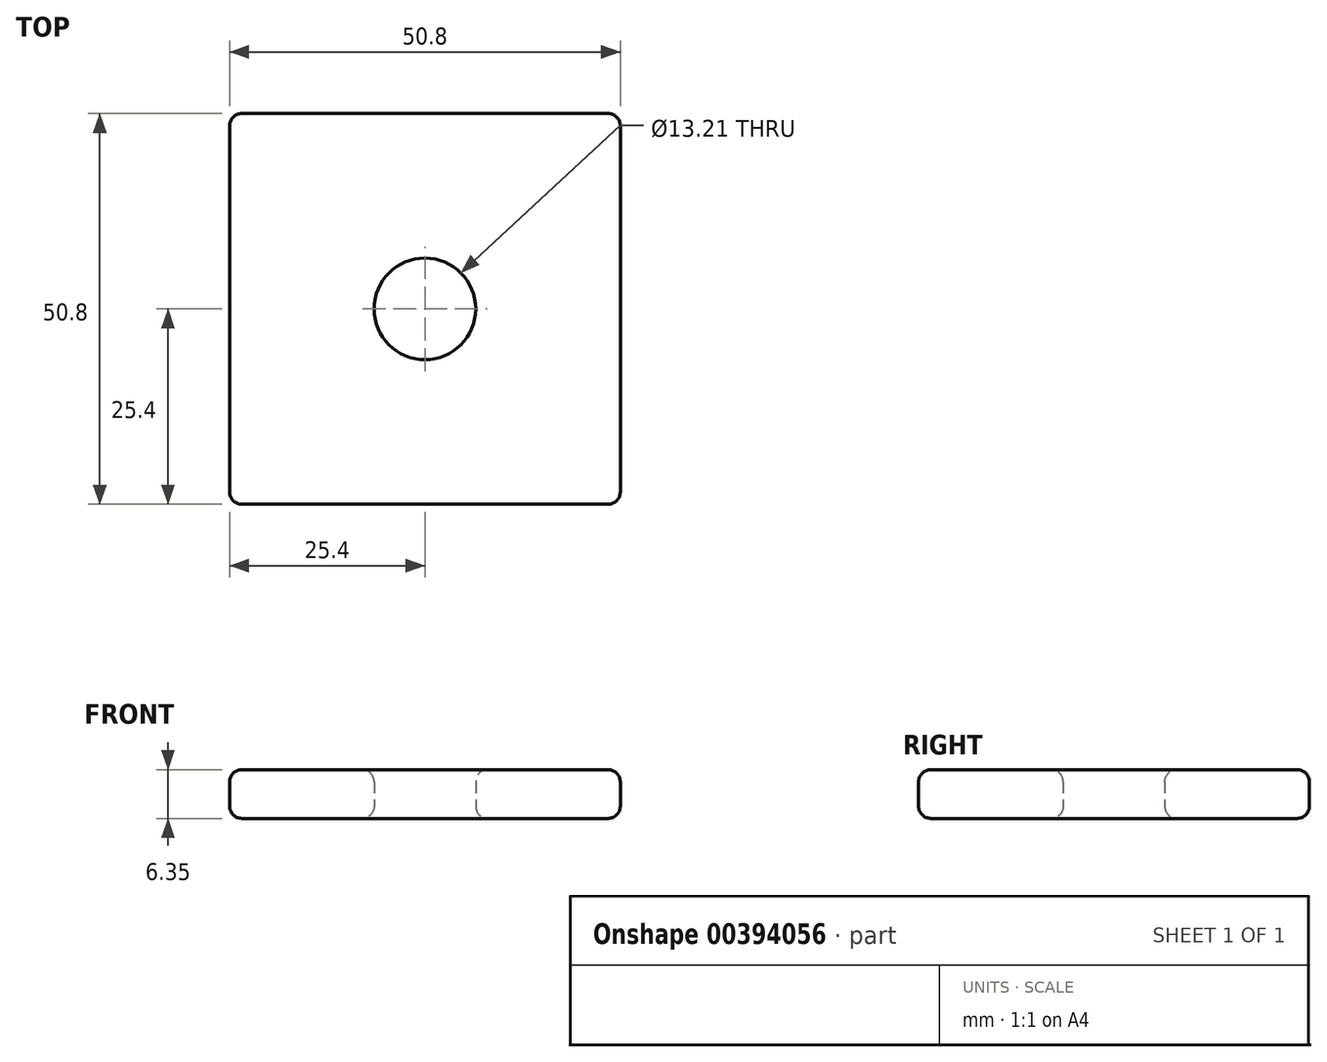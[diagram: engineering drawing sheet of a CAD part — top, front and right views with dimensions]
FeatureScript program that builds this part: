
annotation { "Feature Type Name" : "Feature", "Feature Type Description" : "" }
export const myFeature = defineFeature(function(context is Context, id is Id, definition is map)
    precondition{}
    {
        {
            var Q0;
            Q0=qCreatedBy(makeId("Top.planeOp"),FACE);
            var sketch = newSketch(context, id + "F0", { "sketchPlane" : qUnion([Q0])});
            skLineSegment(sketch, "E0.bottom", {"start": v(-25.4, 25.4) * mm, "end": v(25.4, 25.4) * mm});
            skLineSegment(sketch, "E0.top", {"start": v(-25.4, -25.4) * mm, "end": v(25.4, -25.4) * mm});
            skLineSegment(sketch, "E0.left", {"start": v(-25.4, 25.4) * mm, "end": v(-25.4, -25.4) * mm});
            skLineSegment(sketch, "E0.right", {"start": v(25.4, 25.4) * mm, "end": v(25.4, -25.4) * mm});
            skPoint(sketch, "E0.middle", {"position": v(0, 0) * mm});
            skCircle(sketch, "E1", {"center": v(0, 0) * mm, "radius": 6.6 * mm});
            skSolve(sketch);
        }
        {
            var Q0;
            Q0=makeQuery(id+"F0.imprint","IMPRINT",FACE,{"disambiguationData":[TD([[makeQuery(id+"F0.imprint","IMPRINT",EDGE,{"derivedFrom":sQuery(id+"F0.wireOp",EDGE,"E0.bottom")}),-1.0]])]});
            extrude(context, id + "F1", {"entities" : qUnion([Q0]), "depth" : 6.35 * mm});
        }
        {
            var Q0;
            Q0=makeQuery(id+"F1.opExtrude","SWEPT_EDGE",EDGE,{"disambiguationData":[OSD([sQuery(id+"F0.wireOp",EDGE,"E0.top"),sQuery(id+"F0.wireOp",EDGE,"E0.right")])]});
            var Q1;
            Q1=makeQuery(id+"F1.opExtrude","SWEPT_EDGE",EDGE,{"disambiguationData":[OSD([sQuery(id+"F0.wireOp",EDGE,"E0.bottom"),sQuery(id+"F0.wireOp",EDGE,"E0.right")])]});
            var Q2;
            Q2=makeQuery(id+"F1.opExtrude","SWEPT_EDGE",EDGE,{"disambiguationData":[OSD([sQuery(id+"F0.wireOp",EDGE,"E0.bottom"),sQuery(id+"F0.wireOp",EDGE,"E0.left")])]});
            var Q3;
            Q3=makeQuery(id+"F1.opExtrude","CAP_EDGE",EDGE,{"disambiguationData":[OSD([sQuery(id+"F0.wireOp",EDGE,"E0.bottom")])],"isStart":true});
            var Q4;
            Q4=makeQuery(id+"F1.opExtrude","CAP_EDGE",EDGE,{"disambiguationData":[OSD([sQuery(id+"F0.wireOp",EDGE,"E0.bottom")])],"isStart":false});
            var Q5;
            Q5=makeQuery(id+"F1.opExtrude","CAP_EDGE",EDGE,{"disambiguationData":[OSD([sQuery(id+"F0.wireOp",EDGE,"E0.top")])],"isStart":true});
            var Q6;
            Q6=makeQuery(id+"F1.opExtrude","CAP_EDGE",EDGE,{"disambiguationData":[OSD([sQuery(id+"F0.wireOp",EDGE,"E0.left")])],"isStart":true});
            var Q7;
            Q7=makeQuery(id+"F1.opExtrude","CAP_EDGE",EDGE,{"disambiguationData":[OSD([sQuery(id+"F0.wireOp",EDGE,"E0.right")])],"isStart":true});
            var Q8;
            Q8=makeQuery(id+"F1.opExtrude","CAP_EDGE",EDGE,{"disambiguationData":[OSD([sQuery(id+"F0.wireOp",EDGE,"E0.right")])],"isStart":false});
            var Q9;
            Q9=makeQuery(id+"F1.opExtrude","SWEPT_EDGE",EDGE,{"disambiguationData":[OSD([sQuery(id+"F0.wireOp",EDGE,"E0.top"),sQuery(id+"F0.wireOp",EDGE,"E0.left")])]});
            var Q10;
            Q10=makeQuery(id+"F1.opExtrude","CAP_EDGE",EDGE,{"disambiguationData":[OSD([sQuery(id+"F0.wireOp",EDGE,"E0.top")])],"isStart":false});
            var Q11;
            Q11=makeQuery(id+"F1.opExtrude","CAP_EDGE",EDGE,{"disambiguationData":[OSD([sQuery(id+"F0.wireOp",EDGE,"E0.left")])],"isStart":false});
            var Q12;
            Q12=makeQuery(id+"F1.opExtrude","CAP_EDGE",EDGE,{"disambiguationData":[OSD([sQuery(id+"F0.wireOp",EDGE,"E1")])],"isStart":false});
            var Q13;
            Q13=makeQuery(id+"F1.opExtrude","CAP_EDGE",EDGE,{"disambiguationData":[OSD([sQuery(id+"F0.wireOp",EDGE,"E1")])],"isStart":true});
            fillet(context, id + "F2", {"entities" : qUnion([Q0, Q1, Q2, Q3, Q4, Q5, Q6, Q7, Q8, Q9, Q10, Q11, Q12, Q13]), "radius" : 1.59 * mm, "tangentPropagation" : true, "allowEdgeOverflow" : false});
        }
    });
